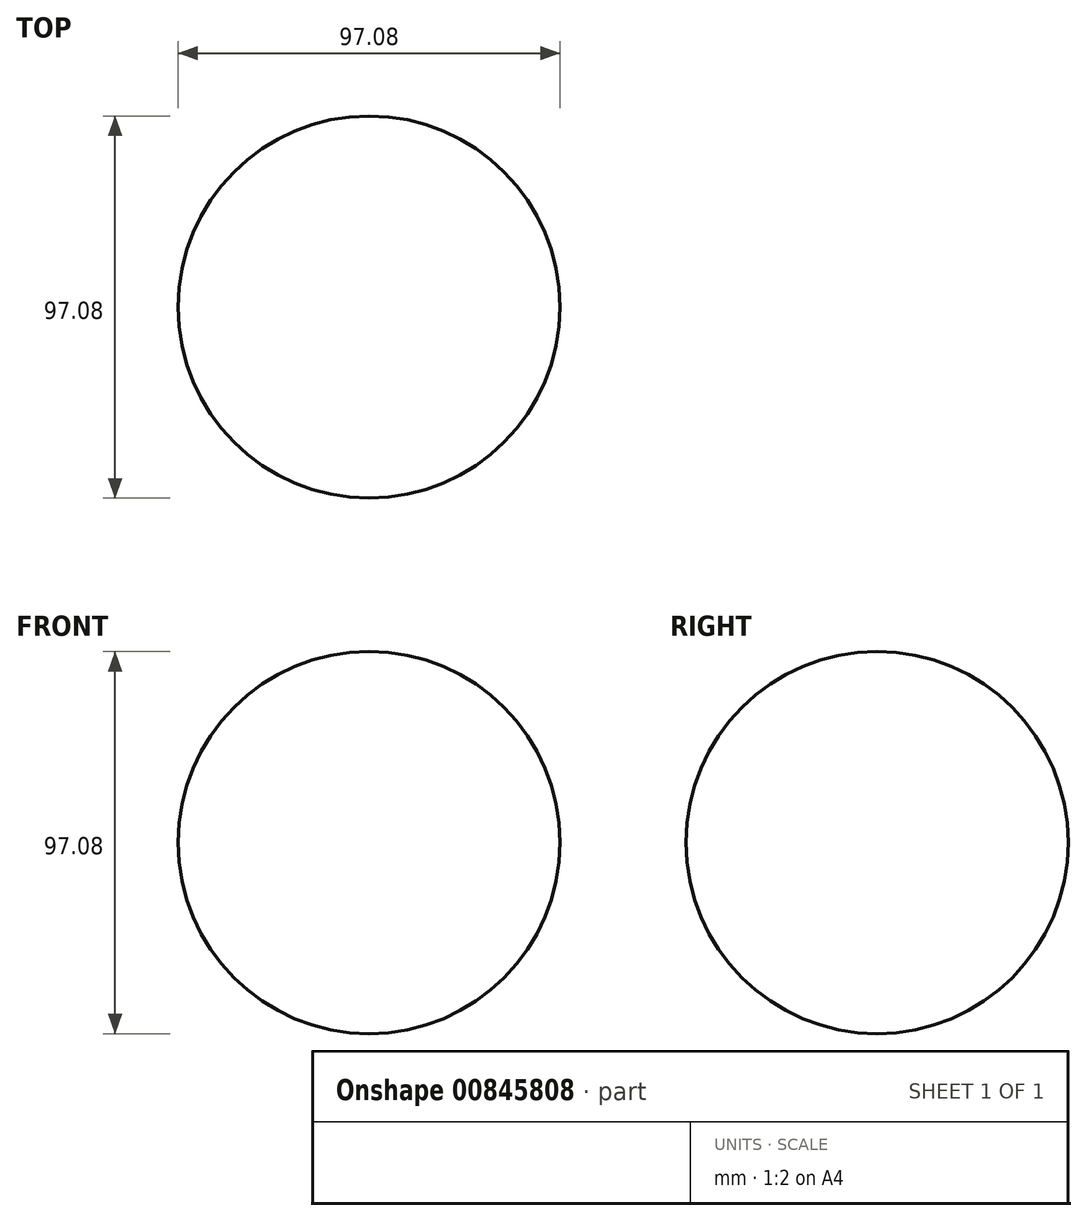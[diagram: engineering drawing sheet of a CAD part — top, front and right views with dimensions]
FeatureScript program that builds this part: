
annotation { "Feature Type Name" : "Feature", "Feature Type Description" : "" }
export const myFeature = defineFeature(function(context is Context, id is Id, definition is map)
    precondition{}
    {
        {
            var Q0;
            Q0=qCreatedBy(makeId("Front.planeOp"),FACE);
            var sketch = newSketch(context, id + "F0", { "sketchPlane" : qUnion([Q0])});
            skCircle(sketch, "E0", {"center": v(0, 0) * mm, "radius": 48.54 * mm});
            skLineSegment(sketch, "E1", {"start": v(0, 67.2) * mm, "end": v(0, -68.72) * mm});
            skSolve(sketch);
        }
        {
            var Q0;
            {var subQ0=sQuery(id+"F0.wireOp",EDGE,"E1");var subQ1=sQuery(id+"F0.wireOp",EDGE,"E0");var subQ2=makeQuery(id+"F0.imprint","INTERSECT",VERTEX,{"disambiguationData":[OD(0.0)],"derivedFrom":[subQ1,subQ0]});Q0=makeQuery(id+"F0.imprint","IMPRINT",FACE,{"disambiguationData":[TD([[makeQuery(id+"F0.imprint","IMPRINT",EDGE,{"disambiguationData":[TD([[subQ2,-1.0]])],"derivedFrom":subQ1}),1.0]])]});}
            var Q1;
            Q1=sQuery(id+"F0.wireOp",EDGE,"E1");
            revolve(context, id + "F1", {"surfaceOperationType" : NewSurfaceOperationType.NEW, "entities" : qUnion([Q0]), "axis" : qUnion([Q1]), "revolveType" : RevolveType.FULL});
        }
    });
